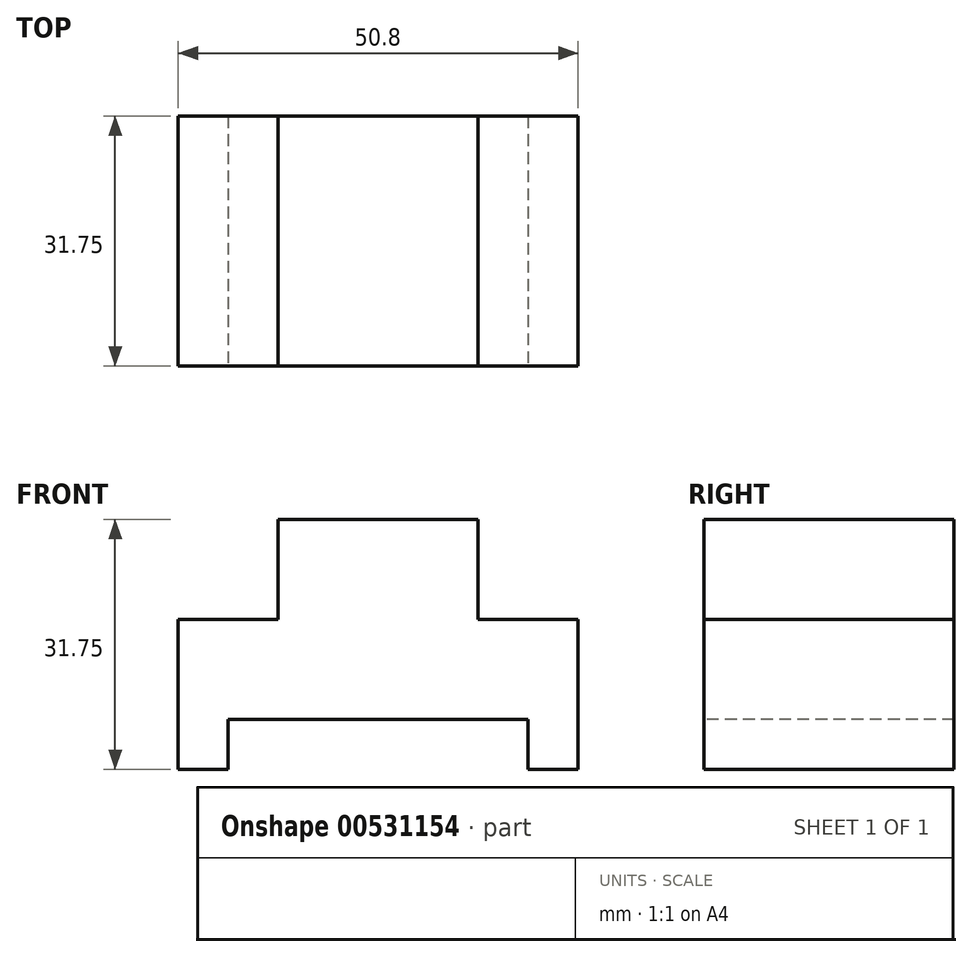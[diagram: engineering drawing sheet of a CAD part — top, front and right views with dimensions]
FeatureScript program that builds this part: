
annotation { "Feature Type Name" : "Feature", "Feature Type Description" : "" }
export const myFeature = defineFeature(function(context is Context, id is Id, definition is map)
    precondition{}
    {
        {
            var Q0;
            Q0=qCreatedBy(makeId("Right.planeOp"),FACE);
            var sketch = newSketch(context, id + "F0", { "sketchPlane" : qUnion([Q0])});
            skLineSegment(sketch, "E0.bottom", {"start": v(0, 0) * mm, "end": v(31.75, 0) * mm});
            skLineSegment(sketch, "E0.top", {"start": v(0, 31.75) * mm, "end": v(31.75, 31.75) * mm});
            skLineSegment(sketch, "E0.left", {"start": v(0, 0) * mm, "end": v(0, 31.75) * mm});
            skLineSegment(sketch, "E0.right", {"start": v(31.75, 0) * mm, "end": v(31.75, 31.75) * mm});
            skSolve(sketch);
        }
        {
            var Q0;
            Q0 = qSketchRegion(id + "F0", true);
            extrude(context, id + "F1", {"entities" : qUnion([Q0]), "depth" : 50.8 * mm, "offsetDistance" : 25.4 * mm});
        }
        {
            var Q0;
            Q0=makeQuery(id+"F1.opExtrude","SWEPT_FACE",FACE,{"disambiguationData":[OSD([sQuery(id+"F0.wireOp",EDGE,"E0.left")])]});
            var sketch = newSketch(context, id + "F2", { "sketchPlane" : qUnion([Q0])});
            skLineSegment(sketch, "E1.bottom", {"start": v(0, 31.75) * mm, "end": v(12.7, 31.75) * mm});
            skLineSegment(sketch, "E1.top", {"start": v(0, 19.05) * mm, "end": v(12.7, 19.05) * mm});
            skLineSegment(sketch, "E1.left", {"start": v(0, 31.75) * mm, "end": v(0, 19.05) * mm});
            skLineSegment(sketch, "E1.right", {"start": v(12.7, 31.75) * mm, "end": v(12.7, 19.05) * mm});
            skLineSegment(sketch, "E2.bottom", {"start": v(50.8, 31.75) * mm, "end": v(38.1, 31.75) * mm});
            skLineSegment(sketch, "E2.top", {"start": v(50.8, 19.05) * mm, "end": v(38.1, 19.05) * mm});
            skLineSegment(sketch, "E2.left", {"start": v(50.8, 31.75) * mm, "end": v(50.8, 19.05) * mm});
            skLineSegment(sketch, "E2.right", {"start": v(38.1, 31.75) * mm, "end": v(38.1, 19.05) * mm});
            skLineSegment(sketch, "E3.bottom", {"start": v(0, 0) * mm, "end": v(6.35, 0) * mm});
            skLineSegment(sketch, "E3.top", {"start": v(0, 6.35) * mm, "end": v(6.35, 6.35) * mm});
            skLineSegment(sketch, "E3.left", {"start": v(0, 0) * mm, "end": v(0, 6.35) * mm});
            skLineSegment(sketch, "E3.right", {"start": v(6.35, 0) * mm, "end": v(6.35, 6.35) * mm});
            skPoint(sketch, "E4.oppositeSnap0", {"position": v(3.17, 6.35) * mm});
            skLineSegment(sketch, "E4.bottom", {"start": v(6.35, 0) * mm, "end": v(44.45, 0) * mm});
            skLineSegment(sketch, "E4.top", {"start": v(6.35, 6.35) * mm, "end": v(44.45, 6.35) * mm});
            skLineSegment(sketch, "E4.right", {"start": v(44.45, 0) * mm, "end": v(44.45, 6.35) * mm});
            skSolve(sketch);
        }
        {
            var Q0;
            Q0=makeQuery(id+"F2.imprint","IMPRINT",FACE,{"disambiguationData":[TD([[makeQuery(id+"F2.imprint","IMPRINT",EDGE,{"derivedFrom":sQuery(id+"F2.wireOp",EDGE,"E1.bottom")}),1.0]])]});
            var Q1;
            Q1=makeQuery(id+"F2.imprint","IMPRINT",FACE,{"disambiguationData":[TD([[makeQuery(id+"F2.imprint","IMPRINT",EDGE,{"derivedFrom":sQuery(id+"F2.wireOp",EDGE,"E2.bottom")}),1.0]])]});
            var Q2;
            Q2=makeQuery(id+"F2.imprint","IMPRINT",FACE,{"disambiguationData":[TD([[makeQuery(id+"F2.imprint","IMPRINT",EDGE,{"derivedFrom":sQuery(id+"F2.wireOp",EDGE,"E4.bottom")}),-1.0]])]});
            extrude(context, id + "F3", {"entities" : qUnion([Q0, Q1, Q2]), "operationType" : NewBodyOperationType.REMOVE, "endBound" : BoundingType.THROUGH_ALL, "oppositeDirection" : true, "depth" : 25.4 * mm, "offsetDistance" : 25.4 * mm});
        }
    });
